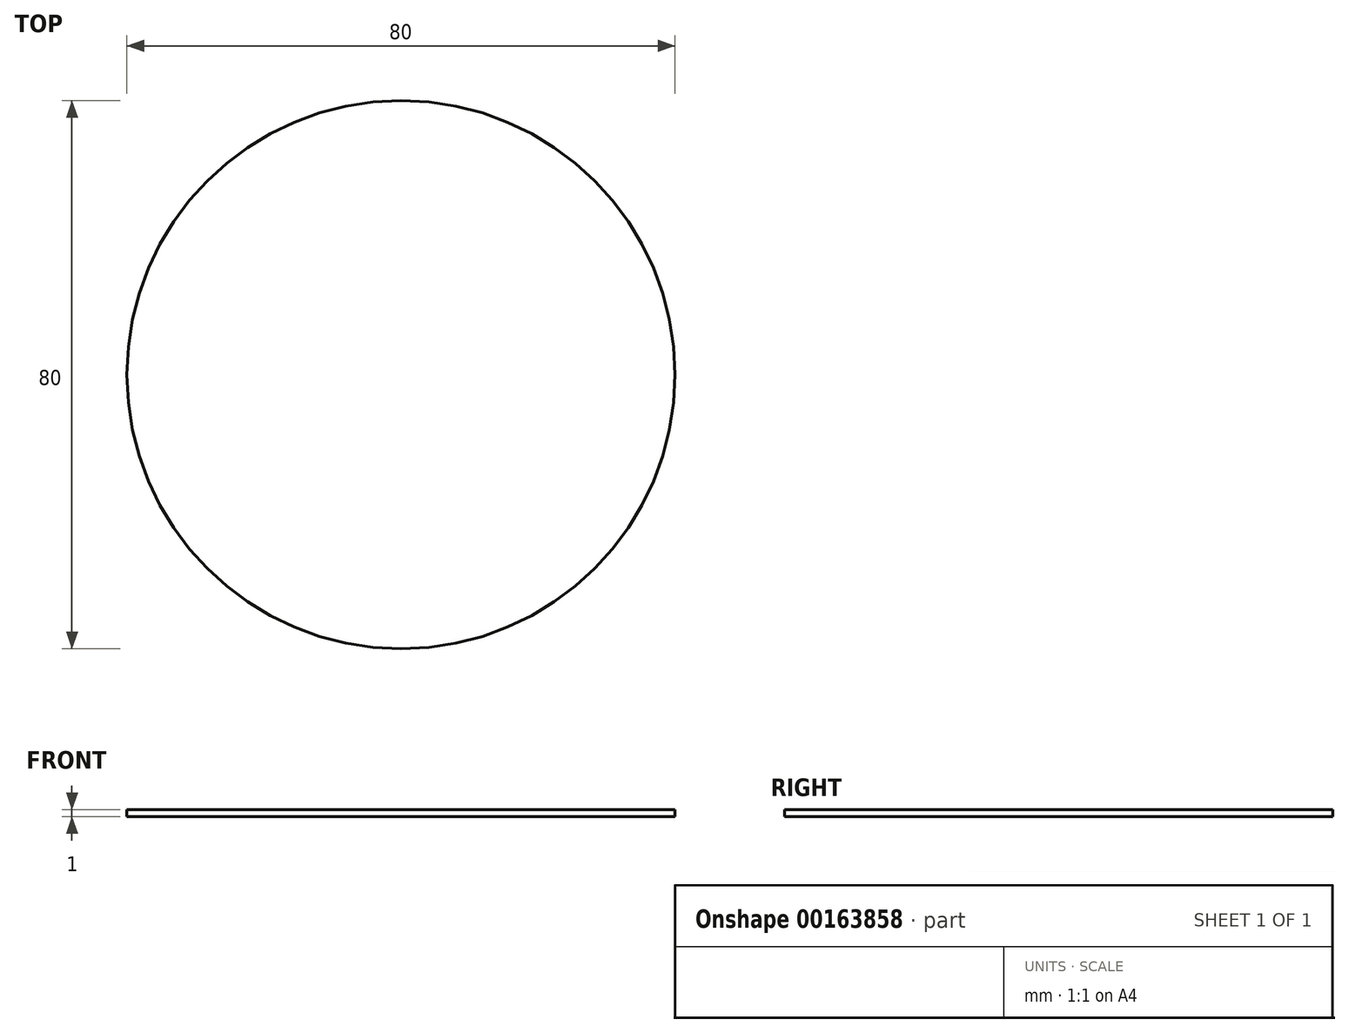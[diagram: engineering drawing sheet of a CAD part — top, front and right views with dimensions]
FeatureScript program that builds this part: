
annotation { "Feature Type Name" : "Feature", "Feature Type Description" : "" }
export const myFeature = defineFeature(function(context is Context, id is Id, definition is map)
    precondition{}
    {
        {
            var Q0;
            Q0=qCreatedBy(makeId("Top.planeOp"),FACE);
            var sketch = newSketch(context, id + "F0", { "sketchPlane" : qUnion([Q0])});
            skCircle(sketch, "E0", {"center": v(0, 0) * mm, "radius": 40 * mm});
            skSolve(sketch);
        }
        {
            var Q0;
            Q0 = qSketchRegion(id + "F0", true);
            extrude(context, id + "F1", {"entities" : qUnion([Q0]), "depth" : 1 * mm});
        }
    });
